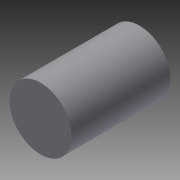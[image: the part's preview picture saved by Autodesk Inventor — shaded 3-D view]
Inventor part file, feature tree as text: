
AUTODESK INVENTOR PART (.ipt)
format: ipt  version: 2018 (Build 220112000, 112)  size: 80,896 bytes
history: native  units: in
note: dims shown in document units (in); Inventor stores cm internally (conversion verified against a paired STEP export)
features: plane x1, extrude x1, sketch x1, reference x1
ambient origin geometry x8: Origin, YZ Plane, XZ Plane, XY Plane, X Axis, Y Axis, Z Axis, Center Point
bodies: Solid1 (feature_tree)
feature tree (4):
  plane  "Work Plane1"
  extrude  "Extrusion1"  Depth=3.358in TaperAngle=0.0deg
  sketch  "Sketch1"  dims[d0=2.11in d1=3.358in d2=0.0in]
  reference  "Reference1"
